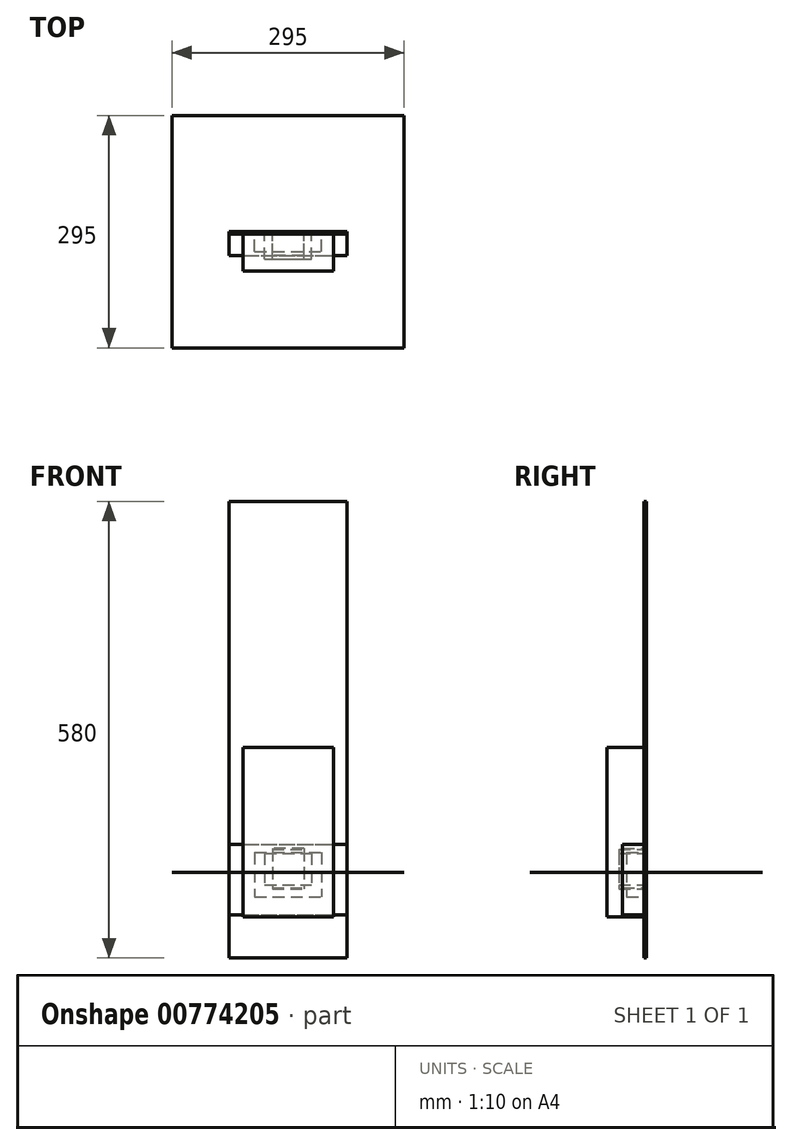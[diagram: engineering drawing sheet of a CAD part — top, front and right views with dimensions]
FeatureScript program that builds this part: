
annotation { "Feature Type Name" : "Feature", "Feature Type Description" : "" }
export const myFeature = defineFeature(function(context is Context, id is Id, definition is map)
    precondition{}
    {
        {
            var Q0;
            Q0=qCreatedBy(makeId("Front.planeOp"),FACE);
            var sketch = newSketch(context, id + "F0", { "sketchPlane" : qUnion([Q0])});
            skLineSegment(sketch, "E0", {"start": v(0, 158.78) * mm, "end": v(-57.5, 158.78) * mm});
            skLineSegment(sketch, "E1", {"start": v(-57.5, 158.78) * mm, "end": v(-57.5, -56.22) * mm});
            skLineSegment(sketch, "E2", {"start": v(-57.5, -56.22) * mm, "end": v(0, -56.22) * mm});
            skLineSegment(sketch, "E3.MirrorCS", {"start": v(57.5, 158.78) * mm, "end": v(57.5, -56.22) * mm});
            skLineSegment(sketch, "E4.MirrorCS", {"start": v(0, 158.78) * mm, "end": v(57.5, 158.78) * mm});
            skLineSegment(sketch, "E5.MirrorCS", {"start": v(57.5, -56.22) * mm, "end": v(0, -56.22) * mm});
            skSolve(sketch);
        }
        {
            var Q0;
            Q0 = qSketchRegion(id + "F0", true);
            extrude(context, id + "F1", {"entities" : qUnion([Q0]), "depth" : 50 * mm, "offsetDistance" : 25 * mm});
        }
        {
            var Q0;
            Q0=qCreatedBy(makeId("Front.planeOp"),FACE);
            var sketch = newSketch(context, id + "F2", { "sketchPlane" : qUnion([Q0])});
            skLineSegment(sketch, "E6", {"start": v(0, 25.4) * mm, "end": v(-42.5, 25.4) * mm});
            skLineSegment(sketch, "E7", {"start": v(-42.5, 25.4) * mm, "end": v(-42.5, -30.6) * mm});
            skLineSegment(sketch, "E8", {"start": v(-42.5, -30.6) * mm, "end": v(0, -30.6) * mm});
            skLineSegment(sketch, "E9.MirrorCS", {"start": v(42.5, -30.6) * mm, "end": v(0, -30.6) * mm});
            skLineSegment(sketch, "E10.MirrorCS", {"start": v(0, 25.4) * mm, "end": v(42.5, 25.4) * mm});
            skLineSegment(sketch, "E11.MirrorCS", {"start": v(42.5, 25.4) * mm, "end": v(42.5, -30.6) * mm});
            skSolve(sketch);
        }
        {
            var Q0;
            Q0 = qSketchRegion(id + "F2", true);
            extrude(context, id + "F3", {"entities" : qUnion([Q0]), "depth" : 25 * mm, "offsetDistance" : 25 * mm});
        }
        {
            var Q0;
            Q0=qCreatedBy(makeId("Front.planeOp"),FACE);
            var sketch = newSketch(context, id + "F4", { "sketchPlane" : qUnion([Q0])});
            skLineSegment(sketch, "E12", {"start": v(0, 24.61) * mm, "end": v(-30, 24.61) * mm});
            skLineSegment(sketch, "E13", {"start": v(-30, 24.61) * mm, "end": v(-30, -15.39) * mm});
            skLineSegment(sketch, "E14", {"start": v(-30, -15.39) * mm, "end": v(0, -15.39) * mm});
            skLineSegment(sketch, "E15.MirrorCS", {"start": v(30, -15.39) * mm, "end": v(0, -15.39) * mm});
            skLineSegment(sketch, "E16.MirrorCS", {"start": v(0, 24.61) * mm, "end": v(30, 24.61) * mm});
            skLineSegment(sketch, "E17.MirrorCS", {"start": v(30, 24.61) * mm, "end": v(30, -15.39) * mm});
            skSolve(sketch);
        }
        {
            var Q0;
            Q0 = qSketchRegion(id + "F4", true);
            extrude(context, id + "F5", {"entities" : qUnion([Q0]), "depth" : 35 * mm, "offsetDistance" : 25 * mm});
        }
        {
            var Q0;
            Q0=qCreatedBy(makeId("Front.planeOp"),FACE);
            var sketch = newSketch(context, id + "F6", { "sketchPlane" : qUnion([Q0])});
            skLineSegment(sketch, "E18", {"start": v(0, 35.98) * mm, "end": v(-75, 35.98) * mm});
            skLineSegment(sketch, "E19", {"start": v(-75, 35.98) * mm, "end": v(-75, -54.02) * mm});
            skLineSegment(sketch, "E20", {"start": v(-75, -54.02) * mm, "end": v(0, -54.02) * mm});
            skLineSegment(sketch, "E21.MirrorCS", {"start": v(0, 35.98) * mm, "end": v(75, 35.98) * mm});
            skLineSegment(sketch, "E22.MirrorCS", {"start": v(75, 35.98) * mm, "end": v(75, -54.02) * mm});
            skLineSegment(sketch, "E23.MirrorCS", {"start": v(75, -54.02) * mm, "end": v(0, -54.02) * mm});
            skSolve(sketch);
        }
        {
            var Q0;
            Q0 = qSketchRegion(id + "F6", true);
            extrude(context, id + "F7", {"entities" : qUnion([Q0]), "depth" : 30 * mm, "offsetDistance" : 25 * mm});
        }
        {
            var Q0;
            Q0=qCreatedBy(makeId("Front.planeOp"),FACE);
            var sketch = newSketch(context, id + "F8", { "sketchPlane" : qUnion([Q0])});
            skLineSegment(sketch, "E24", {"start": v(0, 471.61) * mm, "end": v(-75, 471.61) * mm});
            skLineSegment(sketch, "E25", {"start": v(-75, 471.61) * mm, "end": v(-75, -108.39) * mm});
            skLineSegment(sketch, "E26", {"start": v(-75, -108.39) * mm, "end": v(0, -108.39) * mm});
            skLineSegment(sketch, "E27.MirrorCS", {"start": v(0, 471.61) * mm, "end": v(75, 471.61) * mm});
            skLineSegment(sketch, "E28.MirrorCS", {"start": v(75, -108.39) * mm, "end": v(0, -108.39) * mm});
            skLineSegment(sketch, "E29.MirrorCS", {"start": v(75, 471.61) * mm, "end": v(75, -108.39) * mm});
            skSolve(sketch);
        }
        {
            var Q0;
            Q0 = qSketchRegion(id + "F8", true);
            extrude(context, id + "F9", {"entities" : qUnion([Q0]), "depth" : 3 * mm, "offsetDistance" : 25 * mm});
        }
        {
            var Q0;
            Q0=qCreatedBy(makeId("Front.planeOp"),FACE);
            var sketch = newSketch(context, id + "F10", { "sketchPlane" : qUnion([Q0])});
            skLineSegment(sketch, "E30", {"start": v(0, 30.5) * mm, "end": v(-20, 30.5) * mm});
            skLineSegment(sketch, "E31", {"start": v(-20, 30.5) * mm, "end": v(-20, -19.5) * mm});
            skLineSegment(sketch, "E32", {"start": v(-20, -19.5) * mm, "end": v(0, -19.5) * mm});
            skLineSegment(sketch, "E33.MirrorCS", {"start": v(20, 30.5) * mm, "end": v(20, -19.5) * mm});
            skLineSegment(sketch, "E34.MirrorCS", {"start": v(20, -19.5) * mm, "end": v(0, -19.5) * mm});
            skLineSegment(sketch, "E35.MirrorCS", {"start": v(0, 30.5) * mm, "end": v(20, 30.5) * mm});
            skSolve(sketch);
        }
        {
            var Q0;
            Q0 = qSketchRegion(id + "F10", true);
            extrude(context, id + "F11", {"entities" : qUnion([Q0]), "depth" : 30 * mm, "offsetDistance" : 25 * mm});
        }
        {
            var Q0;
            Q0=qCreatedBy(makeId("Front.planeOp"),FACE);
            var sketch = newSketch(context, id + "F12", { "sketchPlane" : qUnion([Q0])});
            skLineSegment(sketch, "E36", {"start": v(0, 29.43) * mm, "end": v(-20, 29.43) * mm});
            skLineSegment(sketch, "E37", {"start": v(-20, 29.43) * mm, "end": v(-20, -20.57) * mm});
            skLineSegment(sketch, "E38", {"start": v(-20, -20.57) * mm, "end": v(0, -20.57) * mm});
            skLineSegment(sketch, "E39.MirrorCS", {"start": v(20, -20.57) * mm, "end": v(0, -20.57) * mm});
            skLineSegment(sketch, "E40.MirrorCS", {"start": v(0, 29.43) * mm, "end": v(20, 29.43) * mm});
            skLineSegment(sketch, "E41.MirrorCS", {"start": v(20, 29.43) * mm, "end": v(20, -20.57) * mm});
            skSolve(sketch);
        }
        {
            var Q0;
            Q0 = qSketchRegion(id + "F12", true);
            extrude(context, id + "F13", {"entities" : qUnion([Q0]), "depth" : 35 * mm, "offsetDistance" : 25 * mm});
        }
        {
            var Q0;
            Q0=qCreatedBy(makeId("Top.planeOp"),FACE);
            var sketch = newSketch(context, id + "F14", { "sketchPlane" : qUnion([Q0])});
            skLineSegment(sketch, "E42.bottom", {"start": v(147.5, -147.5) * mm, "end": v(-147.5, -147.5) * mm});
            skLineSegment(sketch, "E42.top", {"start": v(147.5, 147.5) * mm, "end": v(-147.5, 147.5) * mm});
            skLineSegment(sketch, "E42.left", {"start": v(147.5, -147.5) * mm, "end": v(147.5, 147.5) * mm});
            skLineSegment(sketch, "E42.right", {"start": v(-147.5, -147.5) * mm, "end": v(-147.5, 147.5) * mm});
            skPoint(sketch, "E42.middle", {"position": v(0, 0) * mm});
            skSolve(sketch);
        }
        {
            var Q0;
            Q0 = qSketchRegion(id + "F14", true);
            extrude(context, id + "F15", {"entities" : qUnion([Q0]), "depth" : .3 * mm, "offsetDistance" : 25 * mm});
        }
    });
